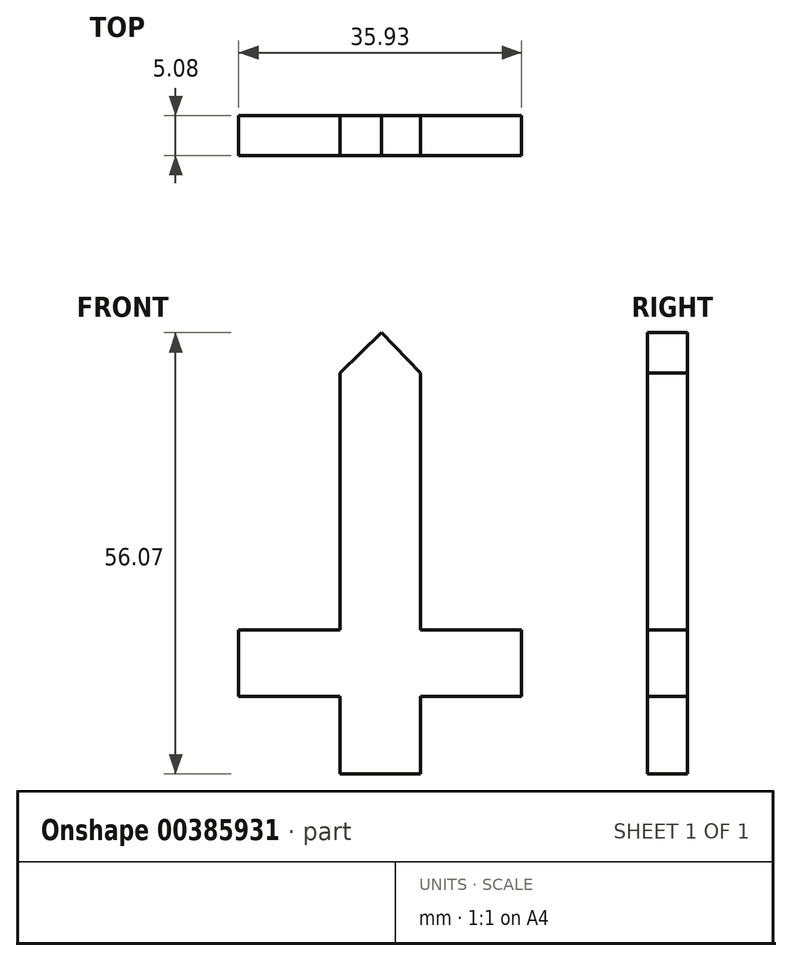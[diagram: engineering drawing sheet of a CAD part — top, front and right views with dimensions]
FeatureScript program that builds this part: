
annotation { "Feature Type Name" : "Feature", "Feature Type Description" : "" }
export const myFeature = defineFeature(function(context is Context, id is Id, definition is map)
    precondition{}
    {
        {
            var Q0;
            Q0=qCreatedBy(makeId("Front.planeOp"),FACE);
            var sketch = newSketch(context, id + "F0", { "sketchPlane" : qUnion([Q0])});
            skLineSegment(sketch, "E0", {"start": v(0, 0) * mm, "end": v(0, 32.64) * mm});
            skLineSegment(sketch, "E1", {"start": v(0, 32.64) * mm, "end": v(5.33, 37.78) * mm});
            skLineSegment(sketch, "E2", {"start": v(5.33, 37.78) * mm, "end": v(10.27, 32.64) * mm});
            skLineSegment(sketch, "E3", {"start": v(10.27, 32.64) * mm, "end": v(10.27, 0) * mm});
            skLineSegment(sketch, "E4", {"start": v(10.27, 0) * mm, "end": v(23.1, 0) * mm});
            skLineSegment(sketch, "E5", {"start": v(23.1, 0) * mm, "end": v(23.1, -8.42) * mm});
            skLineSegment(sketch, "E6", {"start": v(23.1, -8.42) * mm, "end": v(10.27, -8.42) * mm});
            skLineSegment(sketch, "E7", {"start": v(10.27, -8.42) * mm, "end": v(10.27, -18.29) * mm});
            skLineSegment(sketch, "E8", {"start": v(10.27, -18.29) * mm, "end": v(0, -18.29) * mm});
            skLineSegment(sketch, "E9", {"start": v(0, -18.29) * mm, "end": v(0, -8.42) * mm});
            skLineSegment(sketch, "E10", {"start": v(0, -8.42) * mm, "end": v(-12.84, -8.42) * mm});
            skLineSegment(sketch, "E11", {"start": v(-12.84, -8.42) * mm, "end": v(-12.84, 0) * mm});
            skLineSegment(sketch, "E12", {"start": v(-12.84, 0) * mm, "end": v(0, 0) * mm});
            skSolve(sketch);
        }
        {
            var Q0;
            Q0 = qSketchRegion(id + "F0", true);
            extrude(context, id + "F1", {"entities" : qUnion([Q0]), "depth" : 5.08 * mm});
        }
    });
